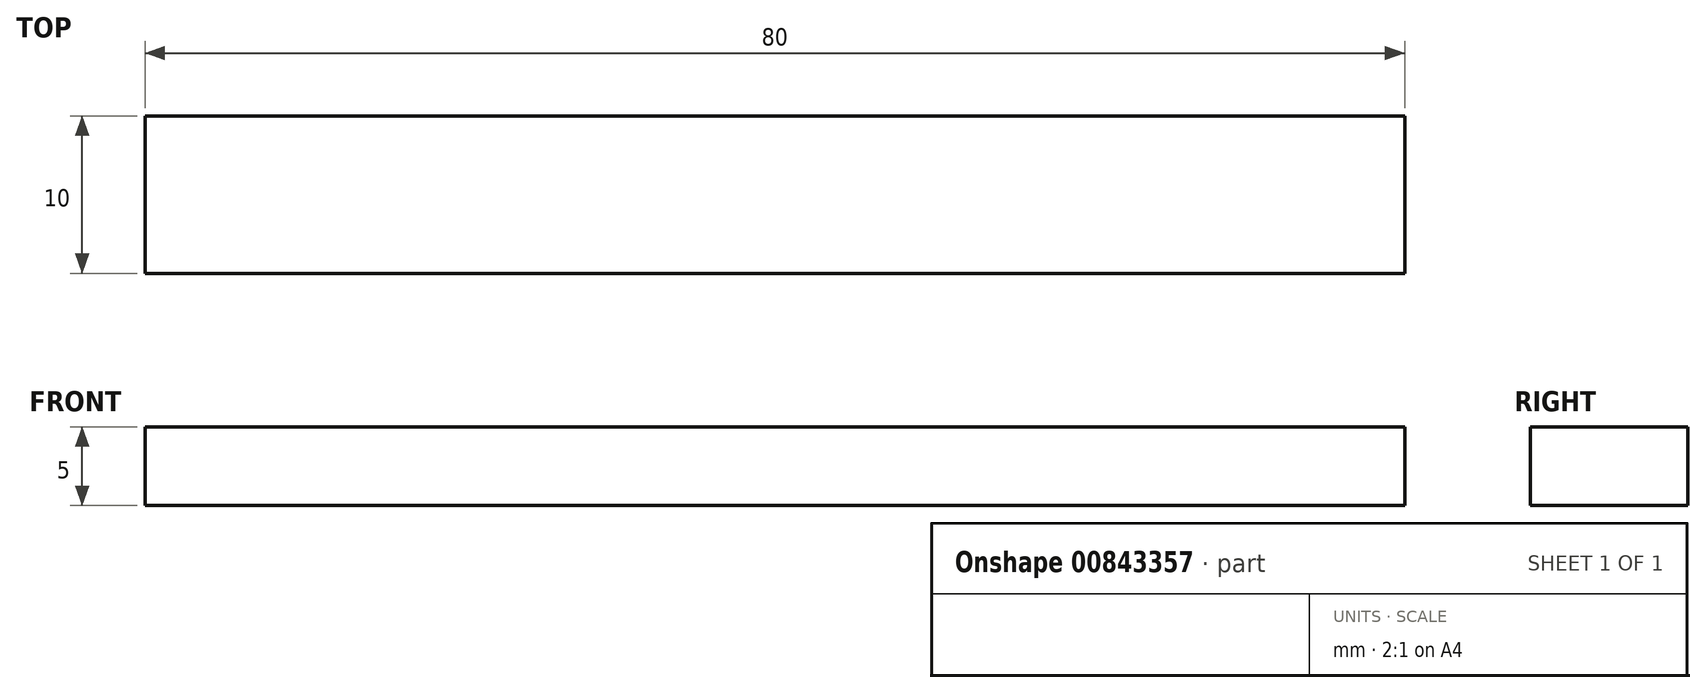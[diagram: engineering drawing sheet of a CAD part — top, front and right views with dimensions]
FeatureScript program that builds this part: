
annotation { "Feature Type Name" : "Feature", "Feature Type Description" : "" }
export const myFeature = defineFeature(function(context is Context, id is Id, definition is map)
    precondition{}
    {
        {
            var Q0;
            Q0=qCreatedBy(makeId("Top.planeOp"),FACE);
            var sketch = newSketch(context, id + "F0", { "sketchPlane" : qUnion([Q0])});
            skLineSegment(sketch, "E0.bottom", {"start": v(-26.57, 10) * mm, "end": v(53.43, 10) * mm});
            skLineSegment(sketch, "E0.top", {"start": v(-26.57, 0) * mm, "end": v(53.43, 0) * mm});
            skLineSegment(sketch, "E0.left", {"start": v(-26.57, 10) * mm, "end": v(-26.57, 0) * mm});
            skLineSegment(sketch, "E0.right", {"start": v(53.43, 10) * mm, "end": v(53.43, 0) * mm});
            skSolve(sketch);
        }
        {
            var Q0;
            Q0=makeQuery(id+"F0.imprint","IMPRINT",FACE,{"disambiguationData":[TD([[makeQuery(id+"F0.imprint","IMPRINT",EDGE,{"derivedFrom":sQuery(id+"F0.wireOp",EDGE,"E0.bottom")}),-1.0]])]});
            extrude(context, id + "F1", {"entities" : qUnion([Q0]), "depth" : 5 * mm, "offsetDistance" : 25 * mm});
        }
    });
